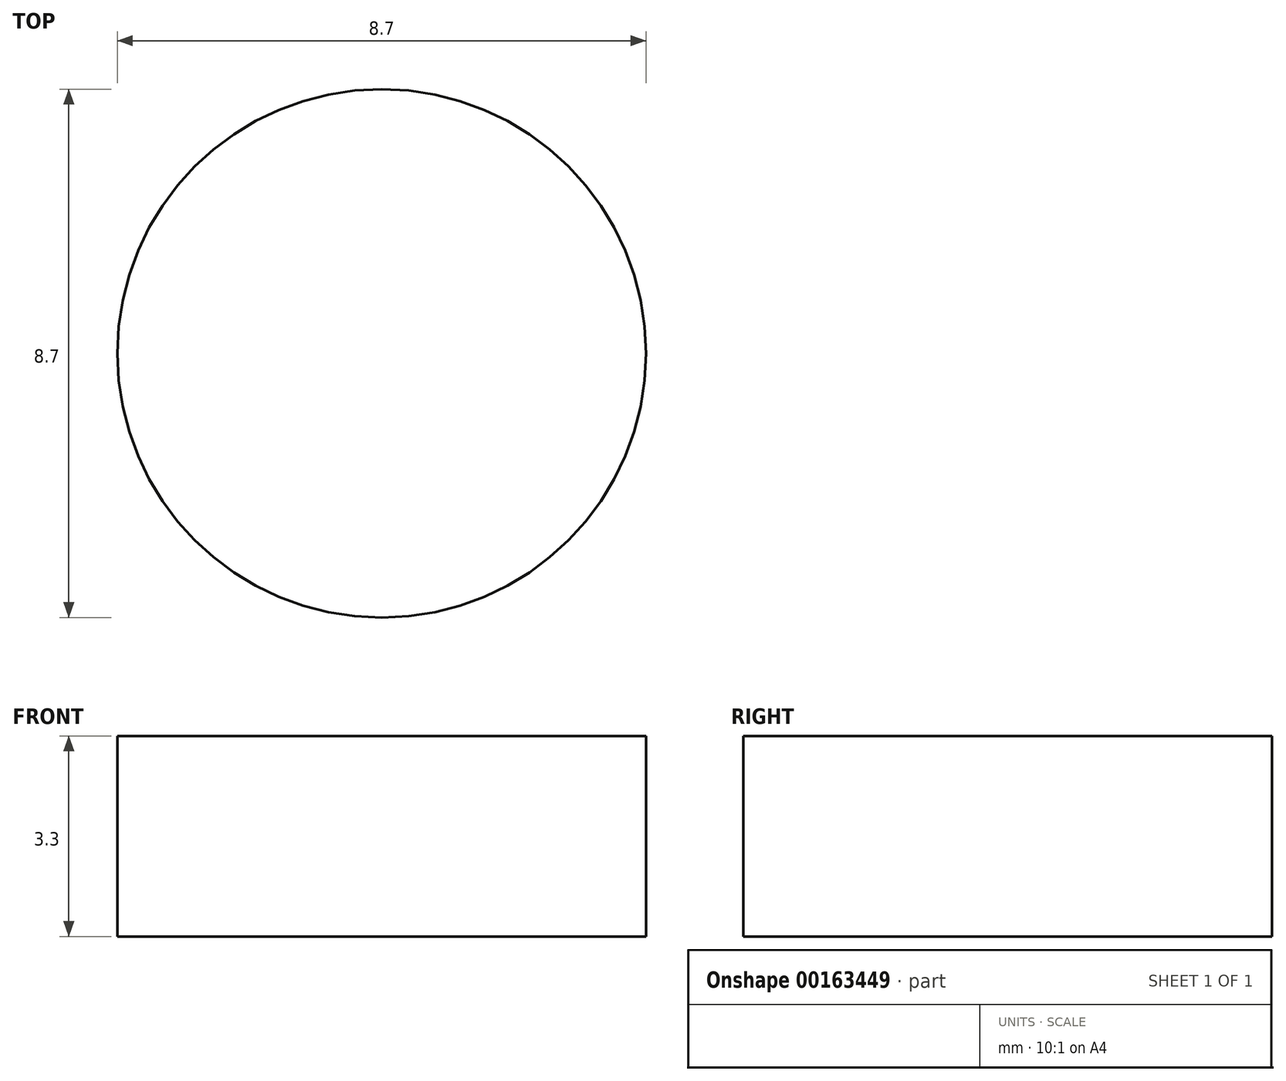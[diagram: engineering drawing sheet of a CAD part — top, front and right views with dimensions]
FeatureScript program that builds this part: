
annotation { "Feature Type Name" : "Feature", "Feature Type Description" : "" }
export const myFeature = defineFeature(function(context is Context, id is Id, definition is map)
    precondition{}
    {
        {
            var Q0;
            Q0=qCreatedBy(makeId("Top.planeOp"),FACE);
            var sketch = newSketch(context, id + "F0", { "sketchPlane" : qUnion([Q0])});
            skCircle(sketch, "E0", {"center": v(0, 0) * mm, "radius": 4.35 * mm});
            skSolve(sketch);
        }
        {
            var Q0;
            Q0=makeQuery(id+"F0.imprint","IMPRINT",FACE,{"disambiguationData":[TD([[makeQuery(id+"F0.imprint","IMPRINT",EDGE,{"derivedFrom":sQuery(id+"F0.wireOp",EDGE,"E0")}),1.0]])]});
            extrude(context, id + "F1", {"entities" : qUnion([Q0]), "depth" : 3.3 * mm});
        }
    });
